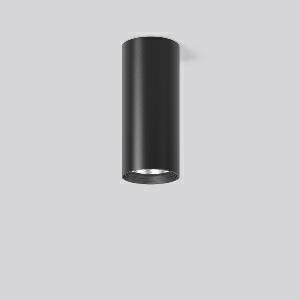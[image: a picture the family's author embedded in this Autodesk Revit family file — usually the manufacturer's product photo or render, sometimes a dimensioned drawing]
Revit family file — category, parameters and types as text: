
# Revit family: heledon_mini_a_931200_003_3_9e63
name_source: partatom
category: Lighting Fixtures
units: mm (PartAtom-declared; Revit-internal decimal feet)

## family parameters
Cut with Voids When Loaded = No
Host = Face
Light Source = No
Part Type = Normal
Room Calculation Point = No
Round Connector Dimension = Use Diameter
Shared = No

## types (1)
- HELEDON mini A (1 x LED Modul 935, 2600 lm, 3500)
    Apparent Load = 20 VA
    Approval mark = CE
    CIE Flux Codes = 100 100 100 100 100
    Color Rendering = 92
    Color Temperature = 3500
    Default Elevation = 1800 mm
    Description = Series: HELEDON mini
Cylindrical surface-mounted downlight. Housing: die-cast aluminium, powder-coated. Internal ceiling frame polycarbonate with bayonet mounting. Black plastic ring and recessed LED to prevent glare from the side. Optical assembly with reflector made of MIRO-Silver with 98% total light reflection for outstanding efficiency - can be changed without tools. Best colour rendering index Ra>90. Suitable for Ceiling mounting. Easy installation with a separate ceiling frame with bayonet mounting and plug connection. Driver integrated. Connected via plug-in connector. High quality converter without flickering and stroboscopic effect. The following accessories can be mounted without use of tools: interchangeable lenses, decorative glasses, honeycomb louvre, clear and frosted diffusers, white interchangeable plastic ring. 
Colour: deep black, matt (RAL 9005)
Diameter: 87 mm
Height: 197 mm
Lamp: LED
Socket: without socket
Colour temperature: 3500K
Colour rendering index (CRI): 92
System power: 20 W
Rated luminous flux: 2600 lm
Luminous efficiency: 130 lm/W
Control gear: Regulated power supply
Protection class: I
Type of protection: IP 20
    Height = 197 mm
    Lamp = 1 x LED Modul 935
    Lamp Light Flux = 2600 lm
    Lamp count = 1
    Length = 87 mm
    Lifetime = 50000 h
    Luminous efficacy = 130 lm/W
    Manufacturer = RZB
    ModVariant = No
    Model = 931200.003.3
    Mounting Place = Ceiling
    Mounting Type = Surface mounted
    Number of Poles = 1
    OnlyDefault = Yes
    Power Factor = 1
    Product Name = HELEDON mini A
    Product group = Surface mounted downlights
    ProductGroupID = 302
    Protection Class = Protection class I
    Protection Degree = IP 20
    RLX_Detail_Level = 1
    RLX_Emergency_Light_Flux = 0 lm
    RLX_Emergency_Type = 0
    RLX_Emergency_Type_DB = No
    RlxData = <blob elided: 107905 chars, md5=7e8c053f>
    Socket = socket
    Standby Power = 0 W
    System Light Flux = 2600 lm
    System Power = 20 W
    Type Comments = Product without accessories
    Type Image = 931188.003.jpg
    URL = http://relux.com
    VarID = ---
    Voltage = 230 V
    Voltage Range = 220-240 V
    Weight = 0.00 kg
    Width = 0 mm  [stored 0 ft]

note: [stored X ft] marks values corroborated as IEEE doubles in the binary element streams (Revit-internal decimal feet)

## geometry (parser evidence)
native form markers: Blend x4, Sweep x11
no freeform markers — native parametric forms only
